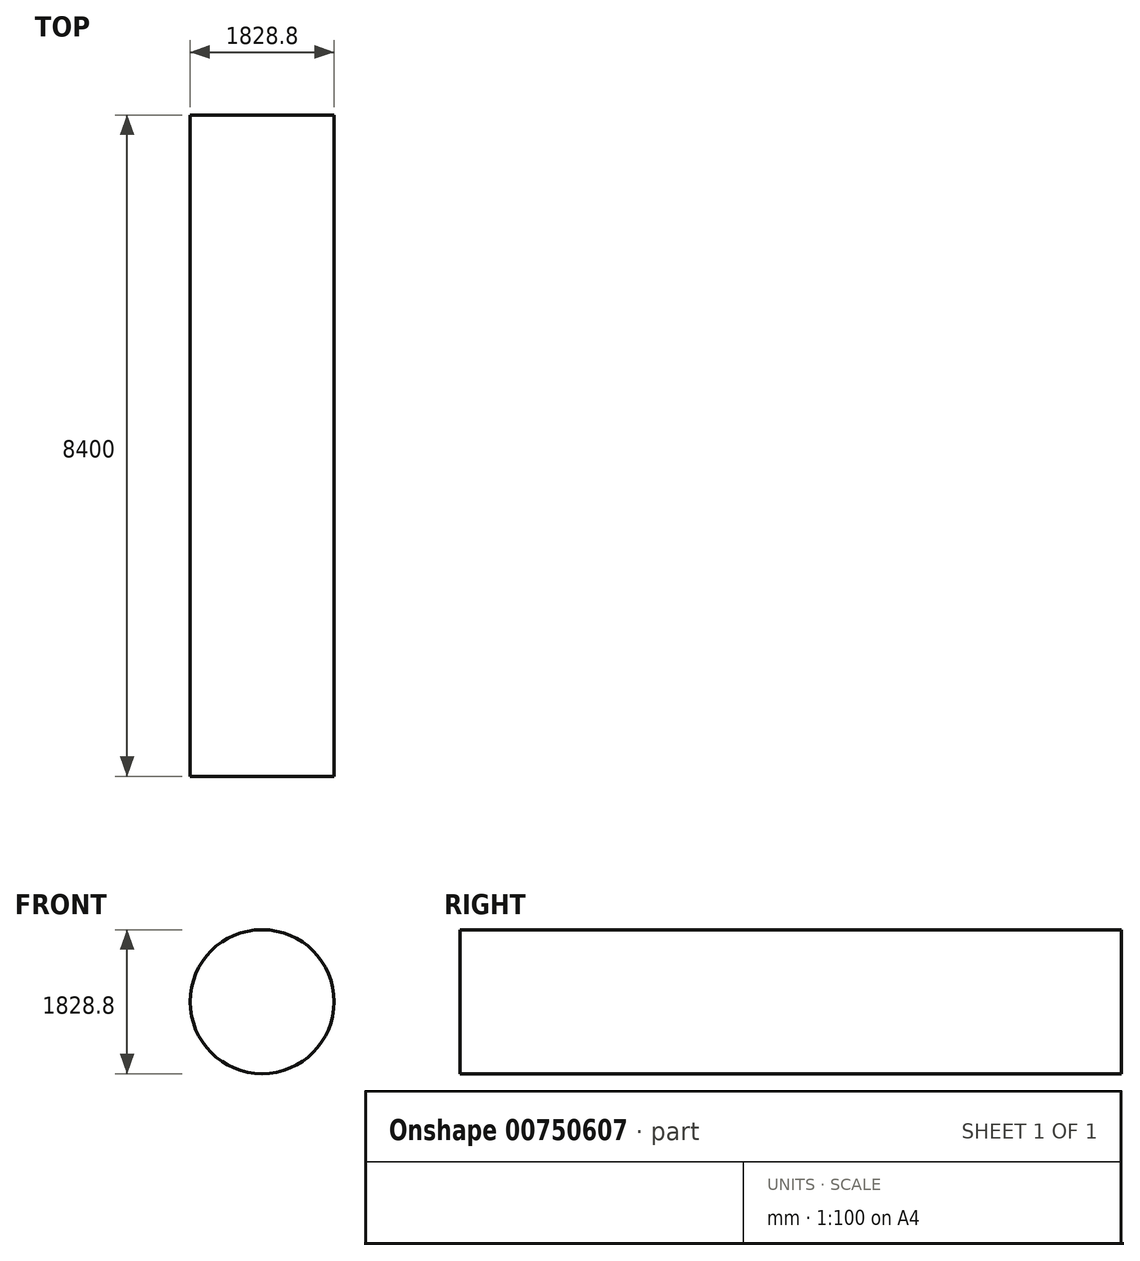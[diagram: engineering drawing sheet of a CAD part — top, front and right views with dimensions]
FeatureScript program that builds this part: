
annotation { "Feature Type Name" : "Feature", "Feature Type Description" : "" }
export const myFeature = defineFeature(function(context is Context, id is Id, definition is map)
    precondition{}
    {
        {
            var Q0;
            Q0=qCreatedBy(makeId("Front.planeOp"),FACE);
            var sketch = newSketch(context, id + "F0", { "sketchPlane" : qUnion([Q0])});
            skCircle(sketch, "E0", {"center": v(0, 0) * mm, "radius": 914.4 * mm});
            skSolve(sketch);
        }
        {
            var Q0;
            Q0=qSketchRegion(id+"F0",true);
            extrude(context, id + "F1", {"entities" : qUnion([Q0]), "depth" : 8400 * mm, "offsetDistance" : 25.4 * mm});
        }
    });
